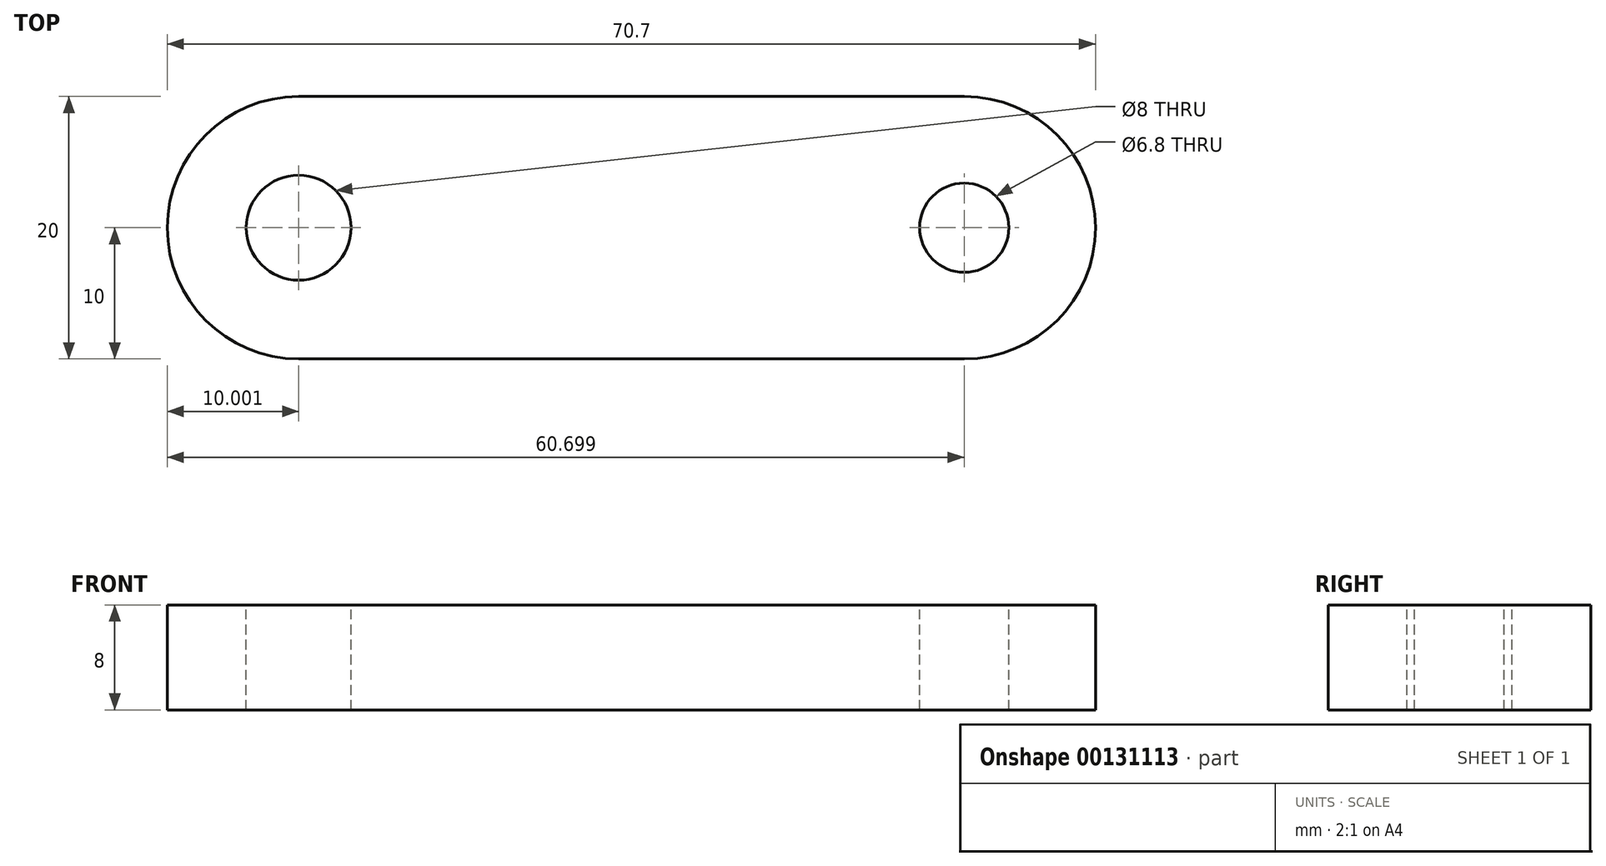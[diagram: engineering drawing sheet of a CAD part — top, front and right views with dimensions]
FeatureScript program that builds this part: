
annotation { "Feature Type Name" : "Feature", "Feature Type Description" : "" }
export const myFeature = defineFeature(function(context is Context, id is Id, definition is map)
    precondition{}
    {
        {
            var Q0;
            Q0=qCreatedBy(makeId("Top.planeOp"),FACE);
            var sketch = newSketch(context, id + "F0", { "sketchPlane" : qUnion([Q0])});
            skLineSegment(sketch, "E0.bottom", {"start": v(35.35, -10) * mm, "end": v(-35.35, -10) * mm});
            skLineSegment(sketch, "E0.top", {"start": v(35.35, 10) * mm, "end": v(-35.35, 10) * mm});
            skLineSegment(sketch, "E0.left", {"start": v(35.35, -10) * mm, "end": v(35.35, 10) * mm});
            skLineSegment(sketch, "E0.right", {"start": v(-35.35, -10) * mm, "end": v(-35.35, 10) * mm});
            skPoint(sketch, "E0.middle", {"position": v(0, 0) * mm});
            skPoint(sketch, "E1", {"position": v(25.35, 0) * mm});
            skPoint(sketch, "E2", {"position": v(-25.35, 0) * mm});
            skSolve(sketch);
        }
        {
            var Q0;
            Q0=makeQuery(id+"F0.imprint","IMPRINT",FACE,{"disambiguationData":[TD([[makeQuery(id+"F0.imprint","IMPRINT",EDGE,{"derivedFrom":sQuery(id+"F0.wireOp",EDGE,"E0.bottom")}),-1.0]])]});
            extrude(context, id + "F1", {"entities" : qUnion([Q0]), "oppositeDirection" : true, "depth" : 8 * mm});
        }
        {
            var Q0;
            Q0=sQuery(id+"F0.wireOp",VERTEX,"E2");
            var Q1;
            Q1=makeQuery(id+"F1.opExtrude","SWEPT_BODY",BODY,{"disambiguationData":[OSD([sQuery(id+"F0.wireOp",EDGE,"E0.bottom"),sQuery(id+"F0.wireOp",EDGE,"E0.top"),sQuery(id+"F0.wireOp",EDGE,"E0.left"),sQuery(id+"F0.wireOp",EDGE,"E0.right")])]});
            hole(context, id + "F2", {"style" : HoleStyle.SIMPLE, "endStyle" : HoleEndStyle.THROUGH, "holeDiameter" : 8 * mm, "locations" : qUnion([Q0]), "scope" : qUnion([Q1]), "isTappedThrough" : true});
        }
        {
            var Q0;
            Q0=sQuery(id+"F0.wireOp",VERTEX,"E1");
            var Q1;
            Q1=makeQuery(id+"F1.opExtrude","SWEPT_BODY",BODY,{"disambiguationData":[OSD([sQuery(id+"F0.wireOp",EDGE,"E0.bottom"),sQuery(id+"F0.wireOp",EDGE,"E0.top"),sQuery(id+"F0.wireOp",EDGE,"E0.left"),sQuery(id+"F0.wireOp",EDGE,"E0.right")])]});
            hole(context, id + "F3", {"style" : HoleStyle.SIMPLE, "endStyle" : HoleEndStyle.THROUGH, "holeDiameter" : 6.8 * mm, "locations" : qUnion([Q0]), "scope" : qUnion([Q1]), "isTappedThrough" : true});
        }
        {
            var Q0;
            Q0=makeQuery(id+"F1.opExtrude","SWEPT_EDGE",EDGE,{"disambiguationData":[OSD([sQuery(id+"F0.wireOp",EDGE,"E0.top"),sQuery(id+"F0.wireOp",EDGE,"E0.left")])]});
            var Q1;
            Q1=makeQuery(id+"F1.opExtrude","SWEPT_EDGE",EDGE,{"disambiguationData":[OSD([sQuery(id+"F0.wireOp",EDGE,"E0.bottom"),sQuery(id+"F0.wireOp",EDGE,"E0.left")])]});
            var Q2;
            Q2=makeQuery(id+"F1.opExtrude","SWEPT_EDGE",EDGE,{"disambiguationData":[OSD([sQuery(id+"F0.wireOp",EDGE,"E0.top"),sQuery(id+"F0.wireOp",EDGE,"E0.right")])]});
            var Q3;
            Q3=makeQuery(id+"F1.opExtrude","SWEPT_EDGE",EDGE,{"disambiguationData":[OSD([sQuery(id+"F0.wireOp",EDGE,"E0.bottom"),sQuery(id+"F0.wireOp",EDGE,"E0.right")])]});
            fillet(context, id + "F4", {"entities" : qUnion([Q0, Q1, Q2, Q3]), "radius" : 10 * mm, "tangentPropagation" : true, "allowEdgeOverflow" : false});
        }
    });
